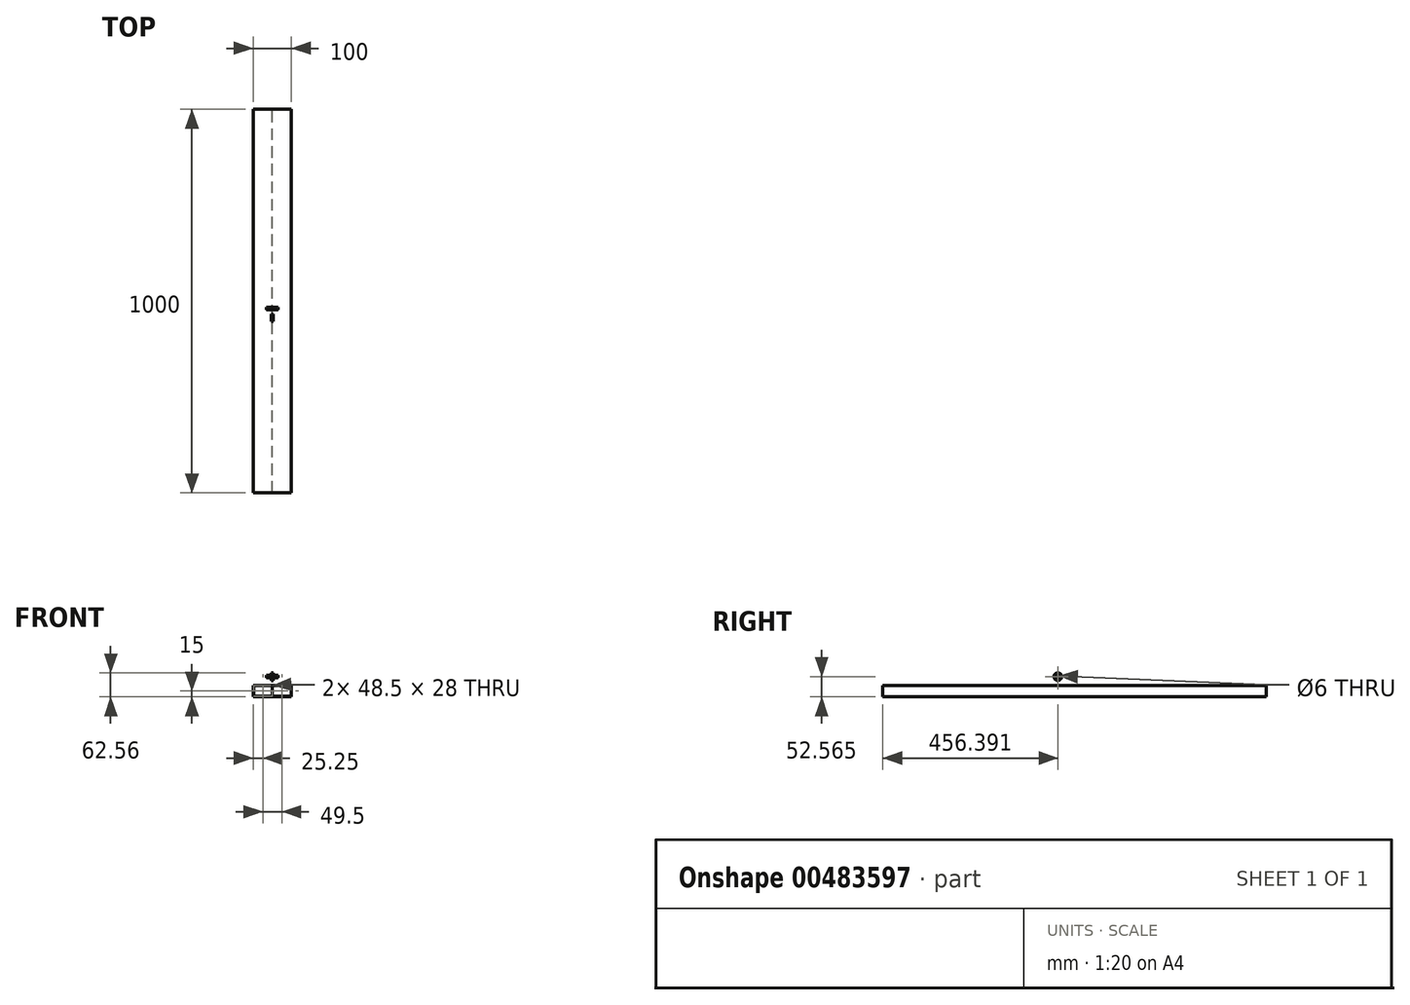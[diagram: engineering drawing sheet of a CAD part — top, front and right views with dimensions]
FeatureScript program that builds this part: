
annotation { "Feature Type Name" : "Feature", "Feature Type Description" : "" }
export const myFeature = defineFeature(function(context is Context, id is Id, definition is map)
    precondition{}
    {
        {
            assignVariable(context, id + "F0", {"name" : "Carriage_Material_Thickness", "anyValue" : 6});
        }
        {
            assignVariable(context, id + "F1", {"name" : "Profile_Length", "anyValue" : 1000});
        }
        {
            assignVariable(context, id + "F2", {"name" : "Axle_Nut_Thickness", "anyValue" : 5});
        }
        {
            assignVariable(context, id + "F3", {"name" : "Axle_Washer_Thickness", "anyValue" : 1});
        }
        {
            assignVariable(context, id + "F4", {"name" : "Bearing_Thickness", "anyValue" : 6});
        }
        {
            var Q0;
            Q0=qCreatedBy(makeId("Front.planeOp"),FACE);
            var sketch = newSketch(context, id + "F5", { "sketchPlane" : qUnion([Q0])});
            skLineSegment(sketch, "E0.bottom", {"start": v(-49, 14) * mm, "end": v(-0.5, 14) * mm});
            skLineSegment(sketch, "E0.top", {"start": v(-49, -14) * mm, "end": v(-0.5, -14) * mm});
            skLineSegment(sketch, "E0.left", {"start": v(-49, 14) * mm, "end": v(-49, -14) * mm});
            skLineSegment(sketch, "E0.right", {"start": v(-0.5, 14) * mm, "end": v(-0.5, -14) * mm});
            skLineSegment(sketch, "E1.bottom", {"start": v(0.5, 14) * mm, "end": v(49, 14) * mm});
            skLineSegment(sketch, "E1.top", {"start": v(0.5, -14) * mm, "end": v(49, -14) * mm});
            skLineSegment(sketch, "E1.left", {"start": v(0.5, 14) * mm, "end": v(0.5, -14) * mm});
            skLineSegment(sketch, "E1.right", {"start": v(49, 14) * mm, "end": v(49, -14) * mm});
            skLineSegment(sketch, "E2.bottom", {"start": v(-50, 15) * mm, "end": v(50, 15) * mm});
            skLineSegment(sketch, "E2.top", {"start": v(-50, -15) * mm, "end": v(50, -15) * mm});
            skLineSegment(sketch, "E2.left", {"start": v(-50, 15) * mm, "end": v(-50, -15) * mm});
            skLineSegment(sketch, "E2.right", {"start": v(50, 15) * mm, "end": v(50, -15) * mm});
            skLineSegment(sketch, "E3", {"start": v(-0.5, -14) * mm, "end": v(0, 0) * mm, "construction": true});
            skLineSegment(sketch, "E4", {"start": v(0, 0) * mm, "end": v(0.5, 14) * mm, "construction": true});
            skLineSegment(sketch, "E5", {"start": v(49, -14) * mm, "end": v(50, -15) * mm, "construction": true});
            skLineSegment(sketch, "E6", {"start": v(-49, 14) * mm, "end": v(-50, 15) * mm, "construction": true});
            skLineSegment(sketch, "E7", {"start": v(-49, -14) * mm, "end": v(-50, -15) * mm, "construction": true});
            skLineSegment(sketch, "E8", {"start": v(49, 14) * mm, "end": v(50, 15) * mm, "construction": true});
            skSolve(sketch);
        }
        {
            var Q0;
            Q0=makeQuery(id+"F5.imprint","IMPRINT",FACE,{"disambiguationData":[TD([[makeQuery(id+"F5.imprint","IMPRINT",EDGE,{"derivedFrom":sQuery(id+"F5.wireOp",EDGE,"E0.bottom")}),1.0]])]});
            extrude(context, id + "F6", {"entities" : qUnion([Q0]), "endBound" : BoundingType.SYMMETRIC, "depth" : (getVariable(context, 'Profile_Length')) * mm});
        }
        {
            var Q0;
            Q0=qCreatedBy(makeId("Right.planeOp"),FACE);
            var sketch = newSketch(context, id + "F7", { "sketchPlane" : qUnion([Q0])});
            skCircle(sketch, "E9", {"center": v(-43.6, 37.56) * mm, "radius": 3 * mm});
            skCircle(sketch, "E10", {"center": v(-43.6, 37.56) * mm, "radius": 10 * mm});
            skSolve(sketch);
        }
        {
            var Q0;
            Q0=makeQuery(id+"F7.imprint","IMPRINT",FACE,{"disambiguationData":[TD([[makeQuery(id+"F7.imprint","IMPRINT",EDGE,{"derivedFrom":sQuery(id+"F7.wireOp",EDGE,"E9")}),-1.0]])]});
            extrude(context, id + "F8", {"entities" : qUnion([Q0]), "endBound" : BoundingType.SYMMETRIC, "depth" : (getVariable(context, 'Bearing_Thickness')) * mm});
        }
        {
            var Q0;
            Q0=qCreatedBy(makeId("Right.planeOp"),FACE);
            var sketch = newSketch(context, id + "F9", { "sketchPlane" : qUnion([Q0])});
            skCircle(sketch, "E11", {"center": v(-19.38, 38.27) * mm, "radius": 3 * mm});
            skSolve(sketch);
        }
        {
            var Q0;
            Q0=makeQuery(id+"F9.imprint","IMPRINT",FACE,{"disambiguationData":[TD([[makeQuery(id+"F9.imprint","IMPRINT",EDGE,{"derivedFrom":sQuery(id+"F9.wireOp",EDGE,"E11")}),1.0]])]});
            extrude(context, id + "F10", {"entities" : qUnion([Q0]), "endBound" : BoundingType.SYMMETRIC, "depth" : (getVariable(context, 'Bearing_Thickness') + 2 * (getVariable(context, 'Carriage_Material_Thickness') + getVariable(context, 'Axle_Washer_Thickness') + getVariable(context, 'Axle_Nut_Thickness'))) * mm});
        }
    });
